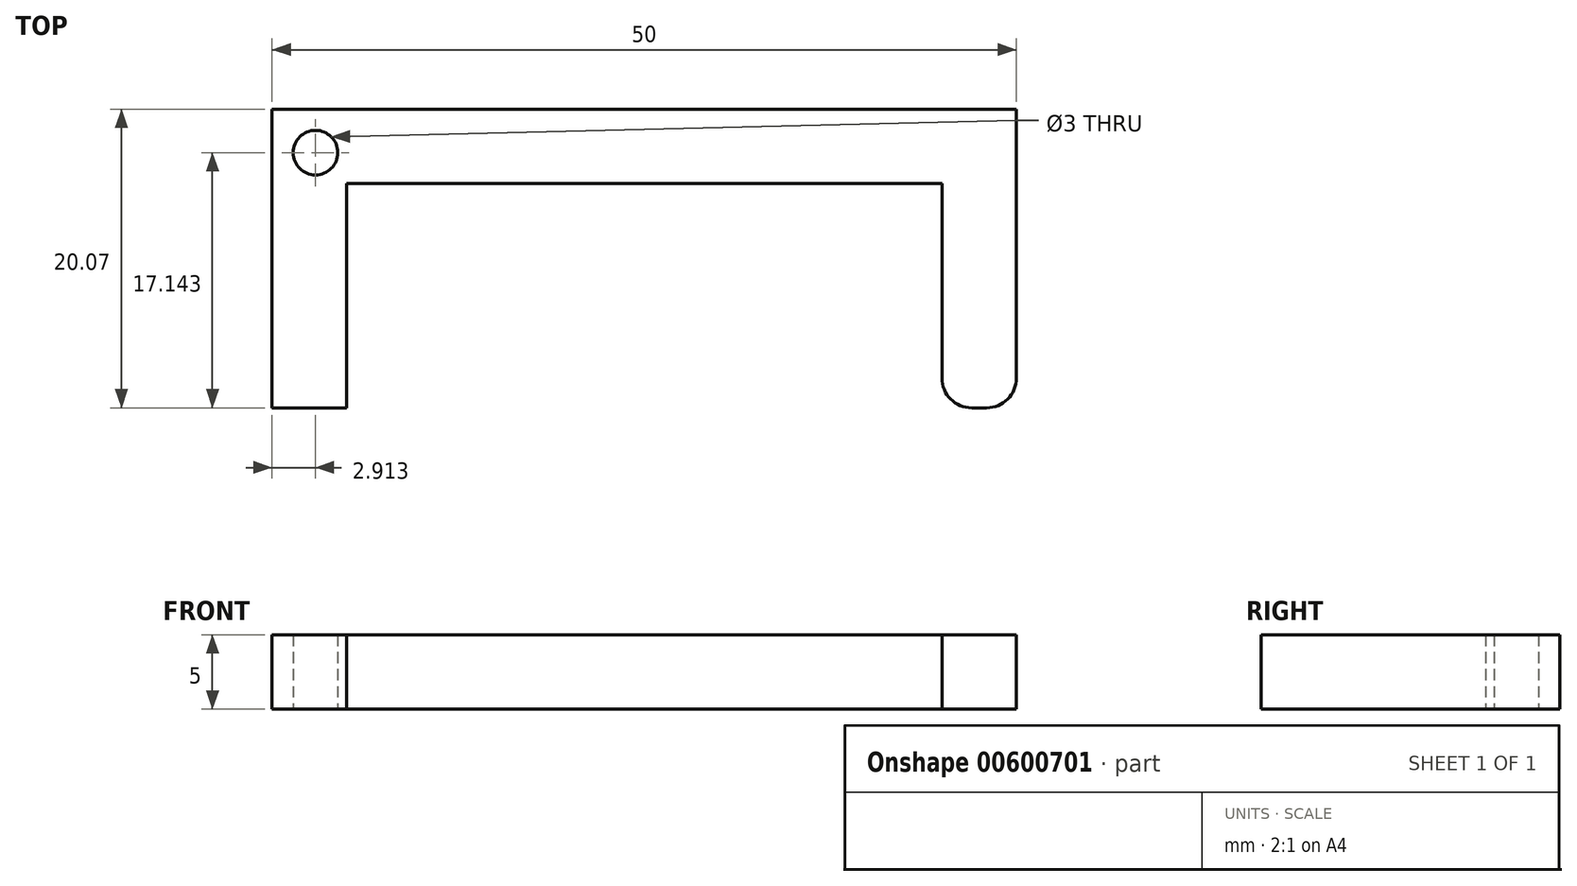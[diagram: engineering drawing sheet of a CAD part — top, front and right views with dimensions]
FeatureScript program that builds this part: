
annotation { "Feature Type Name" : "Feature", "Feature Type Description" : "" }
export const myFeature = defineFeature(function(context is Context, id is Id, definition is map)
    precondition{}
    {
        {
            var Q0;
            Q0=qCreatedBy(makeId("Top.planeOp"),FACE);
            var sketch = newSketch(context, id + "F0", { "sketchPlane" : qUnion([Q0])});
            skLineSegment(sketch, "E0", {"start": v(0, 0) * mm, "end": v(0, 20.07) * mm});
            skLineSegment(sketch, "E1", {"start": v(0, 20.07) * mm, "end": v(50, 20.07) * mm});
            skLineSegment(sketch, "E2", {"start": v(50, 20.07) * mm, "end": v(50, 2) * mm});
            skLineSegment(sketch, "E3", {"start": v(48, 0) * mm, "end": v(47, 0) * mm});
            skLineSegment(sketch, "E4", {"start": v(45, 2) * mm, "end": v(45, 15.07) * mm});
            skLineSegment(sketch, "E5", {"start": v(45, 15.07) * mm, "end": v(5, 15.07) * mm});
            skLineSegment(sketch, "E6", {"start": v(5, 15.07) * mm, "end": v(5, 0) * mm});
            skLineSegment(sketch, "E7", {"start": v(5, 0) * mm, "end": v(0, 0) * mm});
            skPoint(sketch, "E8.visualSharp", {"position": v(45, 0) * mm});
            skArc(sketch, "E8.filletArc", {"start": v(45, 2) * mm, "mid": v(45.59, 0.59) * mm, "end": v(47, 0) * mm});
            skPoint(sketch, "E9.visualSharp", {"position": v(50, 0) * mm});
            skArc(sketch, "E9.filletArc", {"start": v(48, 0) * mm, "mid": v(49.41, 0.59) * mm, "end": v(50, 2) * mm});
            skCircle(sketch, "E10", {"center": v(2.91, 17.14) * mm, "radius": 1.5 * mm});
            skSolve(sketch);
        }
        {
            var Q0;
            Q0=makeQuery(id+"F0.imprint","IMPRINT",FACE,{"disambiguationData":[TD([[makeQuery(id+"F0.imprint","IMPRINT",EDGE,{"derivedFrom":sQuery(id+"F0.wireOp",EDGE,"E0")}),-1.0]])]});
            extrude(context, id + "F1", {"entities" : qUnion([Q0]), "depth" : 5 * mm, "offsetDistance" : 25 * mm});
        }
    });
